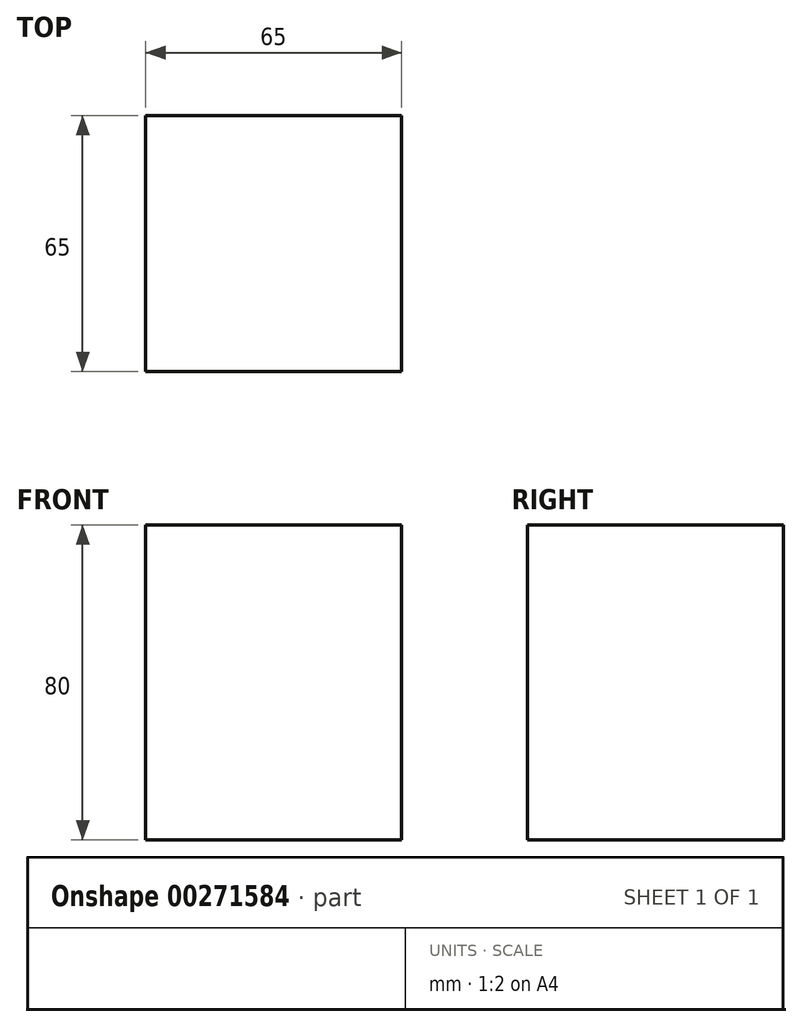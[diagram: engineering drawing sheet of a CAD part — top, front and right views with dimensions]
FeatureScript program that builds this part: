
annotation { "Feature Type Name" : "Feature", "Feature Type Description" : "" }
export const myFeature = defineFeature(function(context is Context, id is Id, definition is map)
    precondition{}
    {
        {
            var Q0;
            Q0=qCreatedBy(makeId("Top.planeOp"),FACE);
            var sketch = newSketch(context, id + "F0", { "sketchPlane" : qUnion([Q0])});
            skLineSegment(sketch, "E0.bottom", {"start": v(31.91, -30.13) * mm, "end": v(-33.09, -30.13) * mm});
            skLineSegment(sketch, "E0.top", {"start": v(31.91, 34.87) * mm, "end": v(-33.09, 34.87) * mm});
            skLineSegment(sketch, "E0.left", {"start": v(31.91, -30.13) * mm, "end": v(31.91, 34.87) * mm});
            skLineSegment(sketch, "E0.right", {"start": v(-33.09, -30.13) * mm, "end": v(-33.09, 34.87) * mm});
            skPoint(sketch, "E0.middle", {"position": v(-0.59, 2.37) * mm});
            skSolve(sketch);
        }
        {
            var Q0;
            Q0 = qSketchRegion(id + "F0", true);
            extrude(context, id + "F1", {"entities" : qUnion([Q0]), "depth" : 80 * mm});
        }
    });
